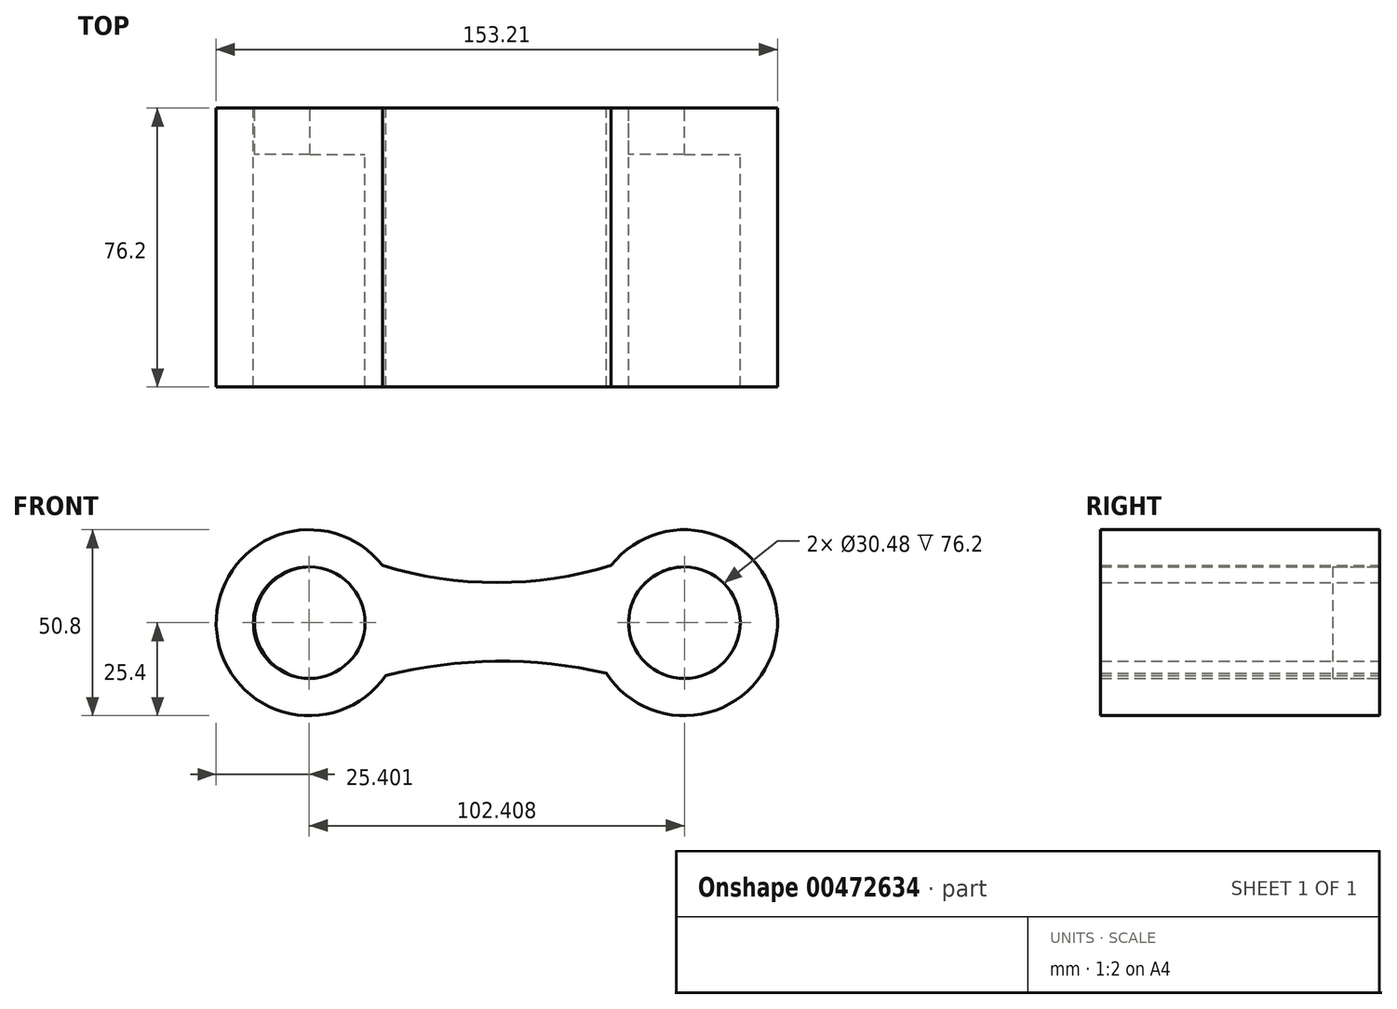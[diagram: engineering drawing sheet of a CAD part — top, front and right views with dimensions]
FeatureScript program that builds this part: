
annotation { "Feature Type Name" : "Feature", "Feature Type Description" : "" }
export const myFeature = defineFeature(function(context is Context, id is Id, definition is map)
    precondition{}
    {
        {
            var Q0;
            Q0=qCreatedBy(makeId("Front.planeOp"),FACE);
            var sketch = newSketch(context, id + "F0", { "sketchPlane" : qUnion([Q0])});
            skCircle(sketch, "E0", {"center": v(-51.63, 0) * mm, "radius": 25.4 * mm});
            skCircle(sketch, "E1", {"center": v(50.78, 0) * mm, "radius": 25.4 * mm});
            skArc(sketch, "E2", {"start": v(-31.63, 15.65) * mm, "mid": v(-0.43, 10.96) * mm, "end": v(30.77, 15.65) * mm});
            skCircle(sketch, "E3", {"center": v(-51.63, 0) * mm, "radius": 15.24 * mm});
            skCircle(sketch, "E4", {"center": v(50.78, 0) * mm, "radius": 15.24 * mm});
            skArc(sketch, "E5", {"start": v(29.44, -13.78) * mm, "mid": v(-0.7, -10.54) * mm, "end": v(-30.76, -14.48) * mm});
            skSolve(sketch);
        }
        {
            var Q0;
            Q0=makeQuery(id+"F0.imprint","IMPRINT",FACE,{"disambiguationData":[TD([[makeQuery(id+"F0.imprint","IMPRINT",EDGE,{"derivedFrom":sQuery(id+"F0.wireOp",EDGE,"E3")}),-1.0]])]});
            var Q1;
            {var subQ0=sQuery(id+"F0.wireOp",EDGE,"E2");Q1=makeQuery(id+"F0.imprint","IMPRINT",FACE,{"disambiguationData":[TD([[makeQuery(id+"F0.imprint","IMPRINT",EDGE,{"derivedFrom":subQ0}),-1.0]])]});}
            var Q2;
            Q2=makeQuery(id+"F0.imprint","IMPRINT",FACE,{"disambiguationData":[TD([[makeQuery(id+"F0.imprint","IMPRINT",EDGE,{"derivedFrom":sQuery(id+"F0.wireOp",EDGE,"E4")}),-1.0]])]});
            extrude(context, id + "F1", {"entities" : qUnion([Q0, Q1, Q2]), "depth" : 76.2 * mm});
        }
        {
            var Q0;
            Q0=qCreatedBy(makeId("Front.planeOp"),FACE);
            var sketch = newSketch(context, id + "F2", { "sketchPlane" : qUnion([Q0])});
            skCircle(sketch, "E6", {"center": v(50.8, 0) * mm, "radius": 15.24 * mm});
            skCircle(sketch, "E7", {"center": v(-51.34, 0) * mm, "radius": 15.24 * mm});
            skSolve(sketch);
        }
        {
            var Q0;
            Q0=makeQuery(id+"F2.imprint","IMPRINT",FACE,{"disambiguationData":[TD([[makeQuery(id+"F2.imprint","IMPRINT",EDGE,{"derivedFrom":sQuery(id+"F2.wireOp",EDGE,"E7")}),1.0]])]});
            var Q1;
            Q1=makeQuery(id+"F2.imprint","IMPRINT",FACE,{"disambiguationData":[TD([[makeQuery(id+"F2.imprint","IMPRINT",EDGE,{"derivedFrom":sQuery(id+"F2.wireOp",EDGE,"E6")}),1.0]])]});
            extrude(context, id + "F3", {"entities" : qUnion([Q0, Q1]), "operationType" : NewBodyOperationType.ADD, "depth" : 12.7 * mm});
        }
        {
            var Q0;
            Q0=qCreatedBy(makeId("Top.planeOp"),FACE);
            var sketch = newSketch(context, id + "F4", { "sketchPlane" : qUnion([Q0])});
            skLineSegment(sketch, "E8.bottom", {"start": v(-22.43, -27.53) * mm, "end": v(23.3, -27.53) * mm});
            skLineSegment(sketch, "E8.top", {"start": v(-22.43, -47.85) * mm, "end": v(23.3, -47.85) * mm});
            skLineSegment(sketch, "E8.left", {"start": v(-22.43, -27.53) * mm, "end": v(-22.43, -47.85) * mm});
            skLineSegment(sketch, "E8.right", {"start": v(23.3, -27.53) * mm, "end": v(23.3, -47.85) * mm});
            skSolve(sketch);
        }
        {
            var Q0;
            Q0=sQuery(id+"F4.wireOp",EDGE,"E8.bottom");
            var Q1;
            Q1=sQuery(id+"F4.wireOp",EDGE,"E8.right");
            var Q2;
            Q2=sQuery(id+"F4.wireOp",EDGE,"E8.top");
            var Q3;
            Q3=sQuery(id+"F4.wireOp",EDGE,"E8.left");
            extrude(context, id + "F5", {"bodyType" : ToolBodyType.SURFACE, "surfaceEntities" : qUnion([Q0, Q1, Q2, Q3]), "depth" : 19.05 * mm});
        }
    });
